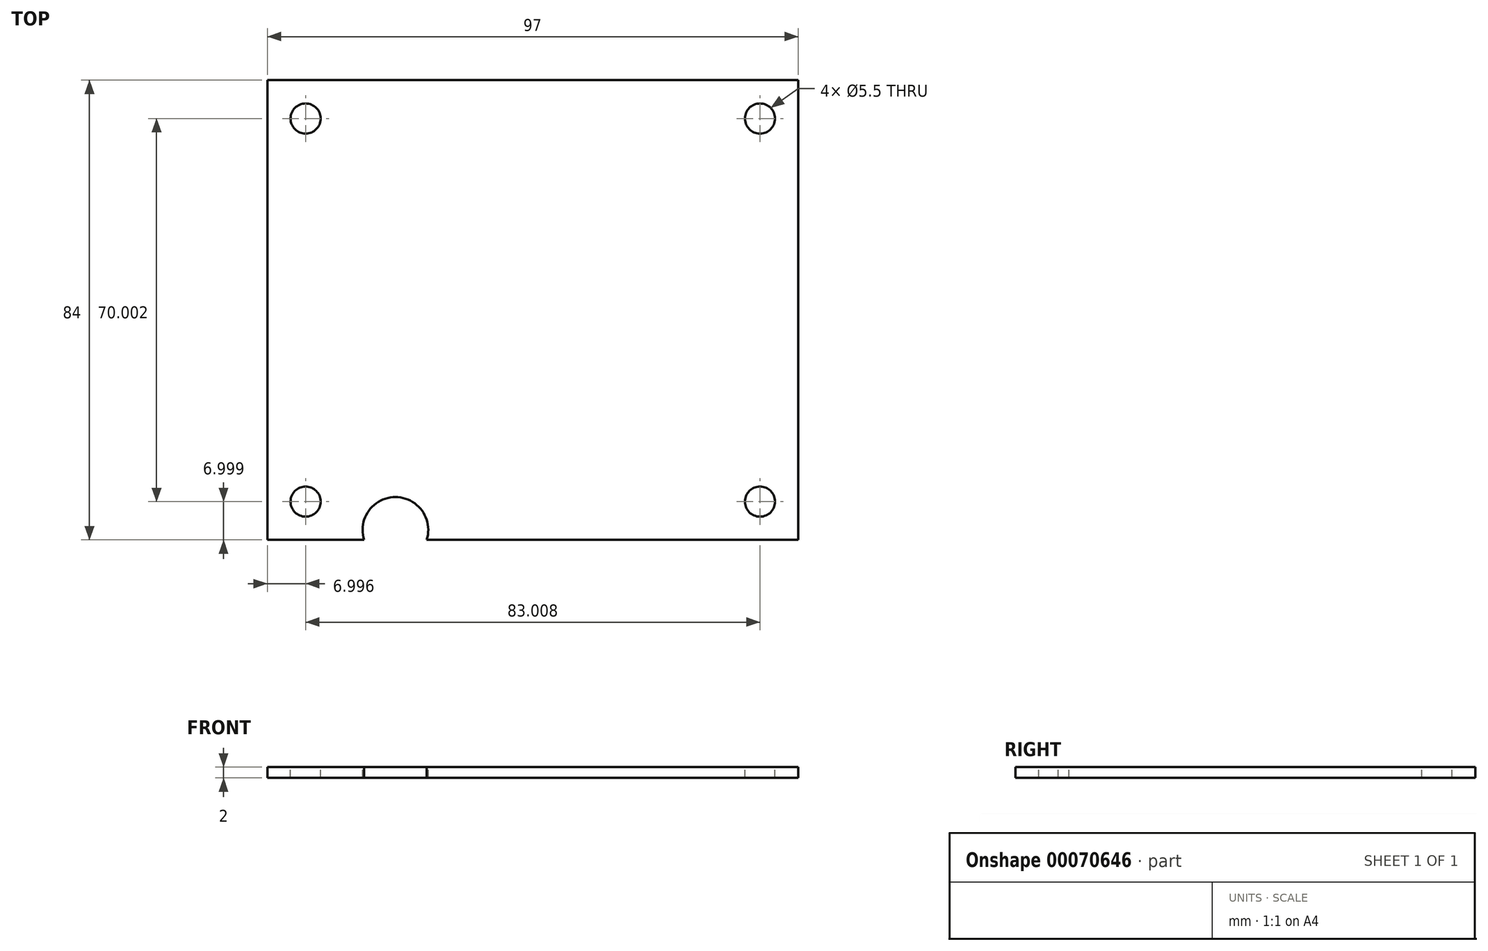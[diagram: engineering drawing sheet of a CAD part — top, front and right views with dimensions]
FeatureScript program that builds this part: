
annotation { "Feature Type Name" : "Feature", "Feature Type Description" : "" }
export const myFeature = defineFeature(function(context is Context, id is Id, definition is map)
    precondition{}
    {
        {
            var Q0;
            Q0=qCreatedBy(makeId("Top.planeOp"),FACE);
            var sketch = newSketch(context, id + "F0", { "sketchPlane" : qUnion([Q0])});
            skLineSegment(sketch, "E0.bottom", {"start": v(-48.5, 42) * mm, "end": v(48.5, 42) * mm});
            skLineSegment(sketch, "E0.top", {"start": v(-48.5, -42) * mm, "end": v(48.5, -42) * mm});
            skLineSegment(sketch, "E0.left", {"start": v(-48.5, 42) * mm, "end": v(-48.5, -42) * mm});
            skLineSegment(sketch, "E0.right", {"start": v(48.5, 42) * mm, "end": v(48.5, -42) * mm});
            skLineSegment(sketch, "E1", {"start": v(-48.5, 42) * mm, "end": v(48.5, -42) * mm, "construction": true});
            skSolve(sketch);
        }
        {
            var Q0;
            Q0=makeQuery(id+"F0.imprint","IMPRINT",FACE,{"disambiguationData":[TD([[makeQuery(id+"F0.imprint","IMPRINT",EDGE,{"derivedFrom":sQuery(id+"F0.wireOp",EDGE,"E0.bottom")}),-1.0]])]});
            extrude(context, id + "F1", {"entities" : qUnion([Q0]), "depth" : 2 * mm});
        }
        {
            var Q0;
            Q0=makeQuery(id+"F1.opExtrude","CAP_FACE",FACE,{"disambiguationData":[OSD([sQuery(id+"F0.wireOp",EDGE,"E0.bottom"),sQuery(id+"F0.wireOp",EDGE,"E0.top"),sQuery(id+"F0.wireOp",EDGE,"E0.left"),sQuery(id+"F0.wireOp",EDGE,"E0.right")])],"isStart":false});
            var sketch = newSketch(context, id + "F2", { "sketchPlane" : qUnion([Q0])});
            skCircle(sketch, "E2", {"center": v(-41.5, 35) * mm, "radius": 2.75 * mm});
            skCircle(sketch, "E3", {"center": v(41.5, 35) * mm, "radius": 2.75 * mm});
            skCircle(sketch, "E4", {"center": v(41.5, -35) * mm, "radius": 2.75 * mm});
            skCircle(sketch, "E5", {"center": v(-41.5, -35) * mm, "radius": 2.75 * mm});
            skLineSegment(sketch, "E6", {"start": v(-41.5, 35) * mm, "end": v(41.5, -35) * mm, "construction": true});
            skLineSegment(sketch, "E7", {"start": v(-41.5, -35) * mm, "end": v(41.5, 35) * mm, "construction": true});
            skSolve(sketch);
        }
        {
            var Q0;
            Q0 = qSketchRegion(id + "F2", true);
            extrude(context, id + "F3", {"entities" : qUnion([Q0]), "operationType" : NewBodyOperationType.REMOVE, "endBound" : BoundingType.UP_TO_NEXT, "oppositeDirection" : true, "depth" : 25.4 * mm});
        }
        {
            var Q0;
            Q0=makeQuery(id+"F1.opExtrude","CAP_FACE",FACE,{"disambiguationData":[OSD([sQuery(id+"F0.wireOp",EDGE,"E0.bottom"),sQuery(id+"F0.wireOp",EDGE,"E0.top"),sQuery(id+"F0.wireOp",EDGE,"E0.left"),sQuery(id+"F0.wireOp",EDGE,"E0.right")])],"isStart":false});
            var sketch = newSketch(context, id + "F4", { "sketchPlane" : qUnion([Q0])});
            skArc(sketch, "E8", {"start": v(-19.38, -42) * mm, "mid": v(-25.1, -34.18) * mm, "end": v(-30.82, -42) * mm});
            skLineSegment(sketch, "E9", {"start": v(-30.82, -42) * mm, "end": v(-19.38, -42) * mm});
            skSolve(sketch);
        }
        {
            var Q0;
            Q0 = qSketchRegion(id + "F4", true);
            extrude(context, id + "F5", {"entities" : qUnion([Q0]), "operationType" : NewBodyOperationType.REMOVE, "endBound" : BoundingType.UP_TO_NEXT, "oppositeDirection" : true, "depth" : 25.4 * mm});
        }
    });
